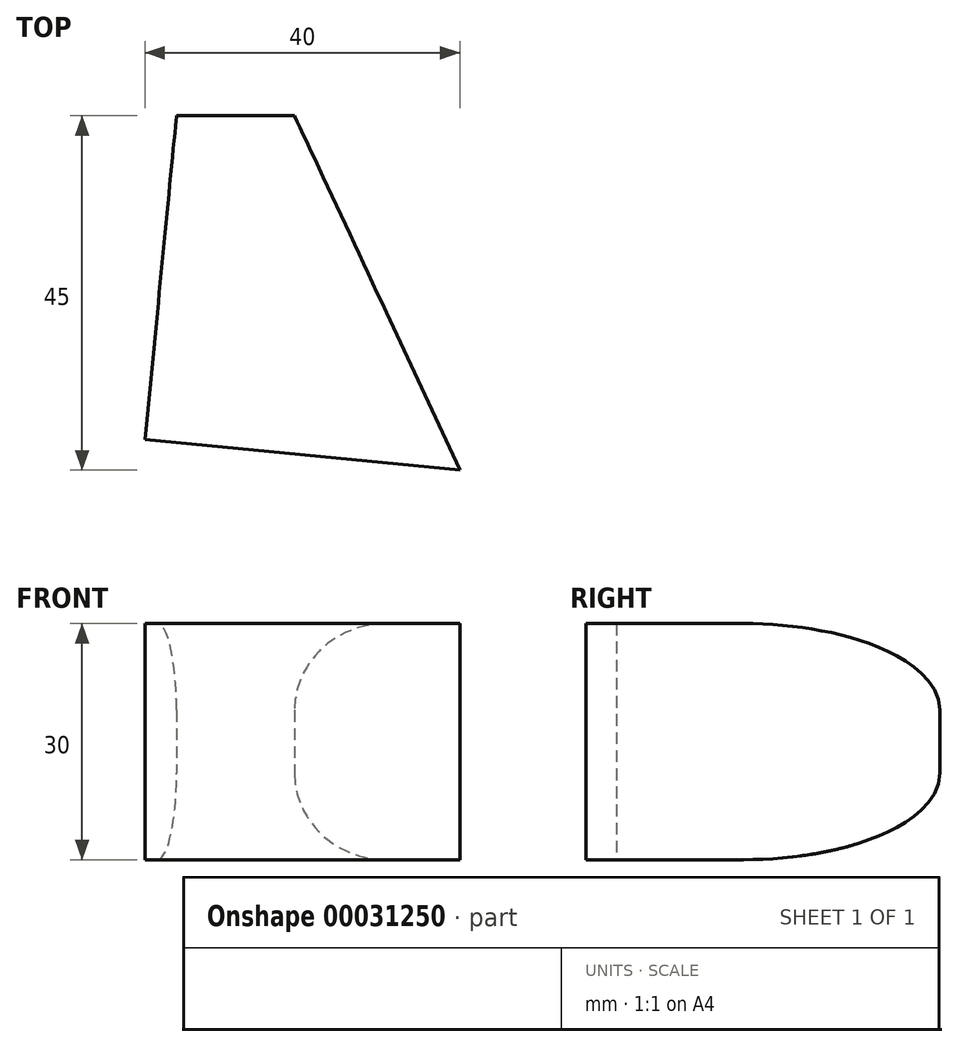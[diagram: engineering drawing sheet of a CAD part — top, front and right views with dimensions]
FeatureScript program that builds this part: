
annotation { "Feature Type Name" : "Feature", "Feature Type Description" : "" }
export const myFeature = defineFeature(function(context is Context, id is Id, definition is map)
    precondition{}
    {
        {
            var Q0;
            Q0=qCreatedBy(makeId("Top.planeOp"),FACE);
            var sketch = newSketch(context, id + "F0", { "sketchPlane" : qUnion([Q0])});
            skLineSegment(sketch, "E0", {"start": v(0, 20) * mm, "end": v(-15, 20) * mm});
            skLineSegment(sketch, "E1", {"start": v(-15, 20) * mm, "end": v(-19, -21.1) * mm});
            skLineSegment(sketch, "E2", {"start": v(-19, -21.1) * mm, "end": v(21, -25) * mm});
            skLineSegment(sketch, "E3", {"start": v(21, -25) * mm, "end": v(0, 20) * mm});
            skSolve(sketch);
        }
        {
            var Q0;
            Q0 = qSketchRegion(id + "F0", true);
            extrude(context, id + "F1", {"entities" : qUnion([Q0]), "depth" : 15 * mm, "hasSecondDirection" : true, "secondDirectionOppositeDirection" : true, "secondDirectionDepth" : 15 * mm});
        }
        {
            var Q0;
            Q0=qCreatedBy(makeId("Right.planeOp"),FACE);
            var sketch = newSketch(context, id + "F2", { "sketchPlane" : qUnion([Q0])});
            skEllipticalArc(sketch, "E4", {});
            skLineSegment(sketch, "E5.0", {"start": v(20, 15) * mm, "end": v(20, -15) * mm, "construction": true});
            skPoint(sketch, "E6", {"position": v(20, -4) * mm});
            skPoint(sketch, "E7", {"position": v(-5, -15) * mm});
            skLineSegment(sketch, "E8", {"start": v(20, -4) * mm, "end": v(-5, -4) * mm, "construction": true});
            skLineSegment(sketch, "E9", {"start": v(-5, -15) * mm, "end": v(-5, -4) * mm, "construction": true});
            skEllipticalArc(sketch, "E10.MirrorCS", {});
            skLineSegment(sketch, "E11", {"start": v(-5, -15) * mm, "end": v(20, -15) * mm});
            skLineSegment(sketch, "E12", {"start": v(20, 15) * mm, "end": v(20, -15) * mm});
            skLineSegment(sketch, "E13", {"start": v(-5, 15) * mm, "end": v(20, 15) * mm});
            const initialGuessF2  = {"E4": [-0.005, -0.004, 1, 0, 0.025, 0.011, 4.71238898038469, 0], "E10.MirrorCS": [-0.005, 0.004, 1, 0, 0.025, 0.011, 0, 1.5707963267948966]};
            skSetInitialGuess(sketch, initialGuessF2);
            skSolve(sketch);
        }
        {
            var Q0;
            Q0 = qSketchRegion(id + "F2", true);
            extrude(context, id + "F3", {"entities" : qUnion([Q0]), "operationType" : NewBodyOperationType.REMOVE, "endBound" : BoundingType.THROUGH_ALL, "oppositeDirection" : true, "depth" : 25 * mm, "hasSecondDirection" : true, "secondDirectionBound" : SecondDirectionBoundingType.THROUGH_ALL, "secondDirectionOppositeDirection" : false, "secondDirectionDepth" : 25 * mm});
        }
    });
